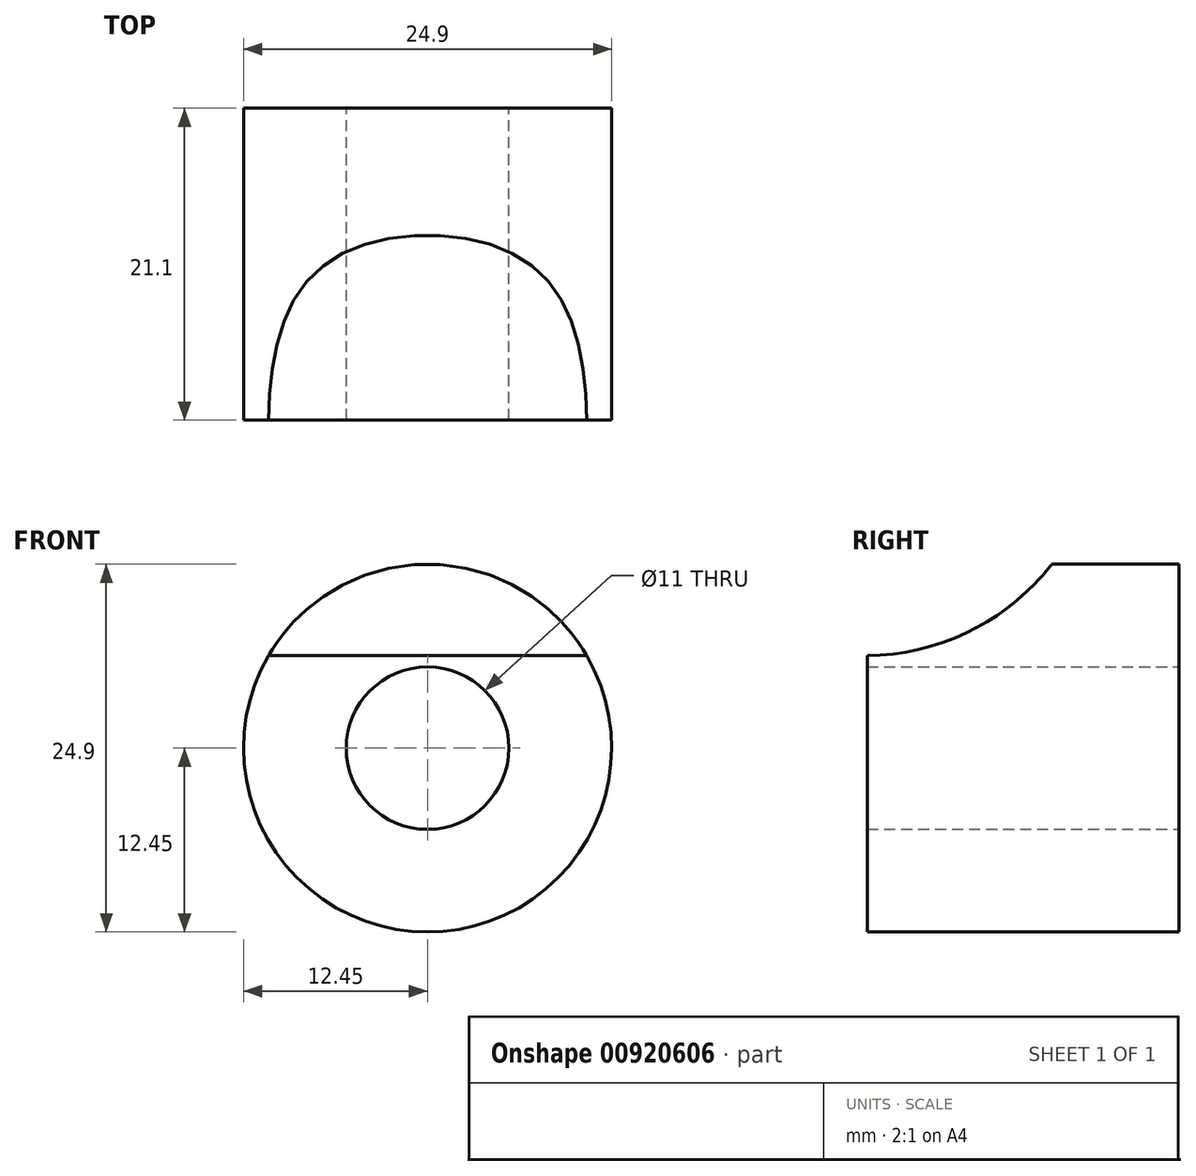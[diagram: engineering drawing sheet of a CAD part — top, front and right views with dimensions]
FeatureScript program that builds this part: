
annotation { "Feature Type Name" : "Feature", "Feature Type Description" : "" }
export const myFeature = defineFeature(function(context is Context, id is Id, definition is map)
    precondition{}
    {
        {
            var Q0;
            Q0=qCreatedBy(makeId("Front.planeOp"),FACE);
            var sketch = newSketch(context, id + "F0", { "sketchPlane" : qUnion([Q0])});
            skCircle(sketch, "E0", {"center": v(0, 0) * mm, "radius": 5.5 * mm});
            skCircle(sketch, "E1", {"center": v(0, 0) * mm, "radius": 12.45 * mm});
            skSolve(sketch);
        }
        {
            var Q0;
            Q0=makeQuery(id+"F0.imprint","IMPRINT",FACE,{"disambiguationData":[TD([[makeQuery(id+"F0.imprint","IMPRINT",EDGE,{"derivedFrom":sQuery(id+"F0.wireOp",EDGE,"E0")}),-1.0]])]});
            extrude(context, id + "F1", {"entities" : qUnion([Q0]), "depth" : 21.1 * mm, "offsetDistance" : 25 * mm});
        }
        {
            var Q0;
            Q0=qCreatedBy(makeId("Right.planeOp"),FACE);
            var sketch = newSketch(context, id + "F2", { "sketchPlane" : qUnion([Q0])});
            skLineSegment(sketch, "E2", {"start": v(0, -12.45) * mm, "end": v(-21.1, -12.45) * mm, "construction": true});
            skLineSegment(sketch, "E3", {"start": v(-21.1, 12.45) * mm, "end": v(-8.6, 12.45) * mm});
            skLineSegment(sketch, "E4.0", {"start": v(-21.1, 6.25) * mm, "end": v(-21.1, 12.45) * mm});
            skPoint(sketch, "E5.orphan", {"position": v(-21.1, -12.45) * mm});
            skArc(sketch, "E6", {"start": v(-21.1, 6.25) * mm, "mid": v(-14.14, 7.92) * mm, "end": v(-8.6, 12.45) * mm});
            skSolve(sketch);
        }
        {
            var Q0;
            Q0=makeQuery(id+"F2.imprint","IMPRINT",FACE,{"disambiguationData":[TD([[makeQuery(id+"F2.imprint","IMPRINT",EDGE,{"derivedFrom":sQuery(id+"F2.wireOp",EDGE,"E3")}),-1.0]])]});
            extrude(context, id + "F3", {"entities" : qUnion([Q0]), "operationType" : NewBodyOperationType.REMOVE, "oppositeDirection" : true, "depth" : 25 * mm, "offsetDistance" : 25 * mm, "symmetric" : true});
        }
    });
